# Revit family: Backflow_Preventer-RP-Zurn_Wilkins-Model_975XL3N-(075-1_inch)
name_source: partatom
category: Pipe Accessories
units: mm (PartAtom-declared; Revit-internal decimal feet)

## family parameters
Always vertical = Yes
Cut with Voids When Loaded = No
OmniClass Number = 23.65.55.14.21
OmniClass Title = Non-Return Valves for Liquid Services
Part Type = Valve - Breaks Into
Round Connector Dimension = Use Radius
Shared = No
Work Plane-Based = No

## types (2) — shared parameters
Assembly Code = D2010.60
BODY FL BOLT HT = 0' - 0 3/16"
BODY FLANGE HT = 0' - 0 1/2"
BODY RIB PATH L1 = 0' - 1 1/8"
BOLT DIA = 0' - 0 5/16"
BV HEX LENGTH = 0' - 0 1/2"
CB L1 = 0' - 0 9/16"
CB L3 = 0' - 0 1/4"
CB L4 = 0' - 0 1/8"
CB TC DIA1 = 0' - 0 3/8"
CB TC DIA2 = 0' - 0 13/16"
CB TC DIA3 = 0' - 0 3/8"
CENTER TO END = 0' - 4 1/4"
DIM A - Inlet center to outlet center = 0' - 8 1/2"
Default Elevation = 0' - 0"
Description = Reduced Pressure Principle Backflow Preventer-N-Pattern
Flow Rate (GPM) = 0 GPM
HANDLE THICKNESS = 0' - 0 1/8"
Hydrostatic Test Pressure = 350.00 psi
LEFT BELND LH DIA = 0' - 1 3/4"
LEFT BELND RH DIA = 0' - 2"
LEFT BLEND START = 0' - 0 7/16"
Left side bend radius = 0' - 1 19/32"
ML LEFT W-1 = 0' - 2 5/8"
Main Material = Paint - Zurn - Bronze
Manufacturer = Zurn Water, LLC
Manufacturer Brand = Zurn Wilkins
Masking hex top = 0' - 1"
Max Working Water Pressure = 175.00 psi
Max Working Water Temperature = 180 °F
Model = 975XL3N
Modified Date = 03/25/26
PIPE RADIUS END = 0' - 3 1/16"
Product Documentation Link = https://files.zurn.com
Product Installation Sheet URL = https://files.zurn.com
Product Page URL = https://www.zurn.com
Product data URL = https://www.bimobject.com
REL COV BOLT LG = 0' - 0 3/16"
REL COV REC WID = 0' - 0 19/32"
REL COVER BOLT C-C = 0' - 1 11/16"
RIGHT LOFT END = 0' - 1 1/16"
RP BTM PIPE DIA = 0' - 0 27/32"
RP BTM PIPE L1 = 0' - 0 3/4"
RP BTM PIPE PLANE = 0' - 0 5/8"
RP END = 0' - 3 7/32"
RP FLANGE HT = 0' - 2 7/32"
RP FLANGE START = 0' - 0 29/32"
RP FLANGE WIDTH = 0' - 2 7/32"
RP LOFT LEFT DIA = 0' - 1 27/32"
RP LOFT RIGHT DIA = 0' - 1 1/2"
RP PIPE 2 = 0' - 1 5/32"
RP PIPE DIA = 0' - 0 29/32"
RP REC THICK = 0' - 0 21/32"
RP REC WIDTH = 0' - 0 27/32"
Repair Parts URL = https://files.zurn.com
TC BASE DIA = 0' - 0 5/8"
TC BASE HT = 0' - 1"
TC CENTER = 0' - 0 3/16"
TC H1 = 0' - 1 1/2"
TC H2 = 0' - 0 1/4"
TC H3 = 0' - 1 1/8"
TC RADIUS 1 = 0' - 0 13/32"
TC RADIUS 2 = 0' - 0 3/16"
TC STEM CENTER = 0' - 0 5/8"
TC STEM DIA = 0' - 0 1/2"
TC STEM HT = 0' - 0 17/32"
URL = https://www.zurn.com

## per-type parameters (varying)
- 34-975XL3N (3/4" 975XL3N): BODY FL HOLE-HOLE=0' - 2 3/8"; BODY FLANGE RADIUS1=0' - 1 1/4"; BODY RIB LINE=0' - 1 9/16"; BODY RIB PATH END=0' - 1 3/8"; BODY RIB THICK=0' - 0 5/32"; BODY RIB WIDTH=0' - 1 1/4"; BODY TC STEM CENTER=0' - 4 1/4"; BV DIA-1=0' - 1 1/8"; BV DIA-2=0' - 1 1/4"; BV DIA-3=0' - 1 1/2"; BV HEX WIDTH=0' - 1 1/4"; BV L1=0' - 0 3/8"; BV L2=0' - 0 5/8"; BV LENGTH=0' - 2 1/2"; BV RIB HT=0' - 0 7/8"; BV RIB START=0' - 0 13/32"; BV RIB THICK=0' - 0 3/8"; BV RIB WIDTH=0' - 1 1/4"; Ball Valve-1=850TUXL_3/4"- 1" : 850TUXL-3/4"; Ball Valve-2=850UXL_3/4"- 1" : 850UXL-3/4"; CB L2=0' - 3"; CB LARGE DIA=0' - 2"; CB SMALL DIA=0' - 1 3/4"; CB START=0' - 1 1/4"; DIM B - Width (Valve center to ball valve handle top)=0' - 1 11/16"; DIM C - Width (Valve center to Valve end)=0' - 1 3/8"; DIM D - Height (Valve Center to top of test cock)=0' - 3 7/32"; DIM E - Height (Valve Center to Bottom of relief valve)=0' - 5 15/32"; HANDLE BASE HT=0' - 1 5/16"; HANDLE H1=0' - 0 1/4"; HANDLE HEIGHT=0' - 0 1/2"; HANDLE NUT WIDTH=0' - 0 11/32"; HANDLE V1=0' - 0 5/8"; HANDLE V2=0' - 1 3/16"; MASKING BTM=0' - 2"; MASKING TOP=0' - 1 1/2"; ML BV DIA-1=0' - 1 1/2"; ML BV DIA-2=0' - 0 3/4"; ML PIPE DIA=0' - 1 1/4"; ML RIGHT W-1=0' - 1 31/32"; ML RIGHT W-2=0' - 2 7/32"; ML RIGHT W-3=0' - 2 31/32"; ML RIGHT W-4=0' - 3 3/32"; MR Body diameter-1=0' - 1 1/2"; MR Body diameter-2=0' - 1 9/32"; MR Body diameter-3=0' - 1 1/8"; MR main body diameter-1=0' - 2 3/4"; MR main body diameter-2=0' - 2 7/32"; MR main body diameter-3=0' - 1 3/4"; MR right end to ball valve handle-1=0' - 0 21/32"; MR right end to ball valve handle-2=0' - 0 23/32"; MR right end to ball valve handle-3=0' - 1 1/32"; MR right end to ball valve handle-4=0' - 1 19/32"; MR right end to ball valve handle-5=0' - 1 29/32"; MR right end to ball valve handle-6=0' - 1 31/32"; MR right end to main body width-1=0' - 2 13/16"; MR right end to main body width-2=0' - 2 31/32"; MR right end to main body width-3=0' - 3 21/32"; MR right end to main body width-4=0' - 3 13/16"; MR valve center to ball valve handle-1=0' - 1 5/8"; MR valve center to ball valve handle-2=0' - 1 1/2"; MR valve center to ball valve handle-3=0' - 1 3/8"; MR valve center to ball valve handle-4=0' - 1 7/32"; Nominal Diameter=0' - 0 3/4"; Nominal Radius=0' - 0 3/8"; PIPE DIA=0' - 1"; Product Weight (lbs)=5; REL COV RED HT=0' - 0 27/32"; REL COVER BOLT DIA=0' - 0 1/4"; RP CENTER=0' - 2 5/16"; RP FLANGE END=0' - 0 7/16"; RP REC HT=0' - 1"; RP START=0' - 2 15/16"; TC1 BASE DIA=0' - 0 1/2"; TC1-CENTER=0' - 0 3/4"; TC2 CENTER=0' - 0 5/8"; TC2 STEM CENTER=0' - 2 3/8"
- 1-975XL3N (1" 975XL3N): BODY FL HOLE-HOLE=0' - 2 23/32"; BODY FLANGE RADIUS1=0' - 1 3/8"; BODY RIB LINE=0' - 1 3/4"; BODY RIB PATH END=0' - 1 1/2"; BODY RIB THICK=0' - 0 3/16"; BODY RIB WIDTH=0' - 1 1/2"; BODY TC STEM CENTER=0' - 4 13/16"; BV DIA-1=0' - 1 1/4"; BV DIA-2=0' - 1 1/2"; BV DIA-3=0' - 1 3/4"; BV HEX WIDTH=0' - 1 1/2"; BV L1=0' - 0 5/8"; BV L2=0' - 1"; BV LENGTH=0' - 3 7/32"; BV RIB HT=0' - 1"; BV RIB START=0' - 0 1/2"; BV RIB THICK=0' - 0 7/16"; BV RIB WIDTH=0' - 1 9/16"; Ball Valve-1=850TUXL_3/4"- 1" : 850TUXL-1"; Ball Valve-2=850UXL_3/4"- 1" : 850UXL-1"; CB L2=0' - 3 1/2"; CB LARGE DIA=0' - 2 1/4"; CB SMALL DIA=0' - 1 7/8"; CB START=0' - 1 1/2"; DIM B - Width (Valve center to ball valve handle top)=0' - 2 5/16"; DIM C - Width (Valve center to Valve end)=0' - 1 9/16"; DIM D - Height (Valve Center to top of test cock)=0' - 3 7/16"; DIM E - Height (Valve Center to Bottom of relief valve)=0' - 7 7/16"; HANDLE BASE HT=0' - 1 1/2"; HANDLE H1=0' - 0 5/16"; HANDLE HEIGHT=0' - 0 7/8"; HANDLE NUT WIDTH=0' - 0 9/16"; HANDLE V1=0' - 0 7/8"; HANDLE V2=0' - 1 1/2"; MASKING BTM=0' - 2 1/4"; MASKING TOP=0' - 1 3/4"; ML BV DIA-1=0' - 1 3/4"; ML BV DIA-2=0' - 1 1/8"; ML PIPE DIA=0' - 1 21/32"; ML RIGHT W-1=0' - 1 1/2"; ML RIGHT W-2=0' - 1 3/4"; ML RIGHT W-3=0' - 2 9/16"; ML RIGHT W-4=0' - 2 11/16"; MR Body diameter-1=0' - 1 3/4"; MR Body diameter-2=0' - 1 1/2"; MR Body diameter-3=0' - 1 1/4"; MR main body diameter-1=0' - 3 1/8"; MR main body diameter-2=0' - 2 1/4"; MR main body diameter-3=0' - 1 25/32"; MR right end to ball valve handle-1=0' - 0 11/16"; MR right end to ball valve handle-2=0' - 0 3/4"; MR right end to ball valve handle-3=0' - 1 1/8"; MR right end to ball valve handle-4=0' - 2 1/16"; MR right end to ball valve handle-5=0' - 2 7/16"; MR right end to ball valve handle-6=0' - 2 1/2"; MR right end to main body width-1=0' - 3 7/32"; MR right end to main body width-2=0' - 3 3/8"; MR right end to main body width-3=0' - 4 3/32"; MR right end to main body width-4=0' - 4 9/32"; MR valve center to ball valve handle-1=0' - 1 7/8"; MR valve center to ball valve handle-2=0' - 1 3/4"; MR valve center to ball valve handle-3=0' - 1 9/16"; MR valve center to ball valve handle-4=0' - 1 13/32"; Nominal Diameter=0' - 1"; Nominal Radius=0' - 0 1/2"; PIPE DIA=0' - 1 1/4"; Product Weight (lbs)=7; REL COV RED HT=0' - 0 29/32"; REL COVER BOLT DIA=0' - 0 7/32"; RP CENTER=0' - 2 13/32"; RP FLANGE END=0' - 0 15/32"; RP REC HT=0' - 1 1/16"; RP START=0' - 3 7/8"; TC1 BASE DIA=0' - 0 5/8"; TC1-CENTER=0' - 0 7/8"; TC2 CENTER=0' - 0 3/4"; TC2 STEM CENTER=0' - 2 9/16"

## geometry (parser evidence)
native form markers: Sweep x12
no freeform markers — native parametric forms only
